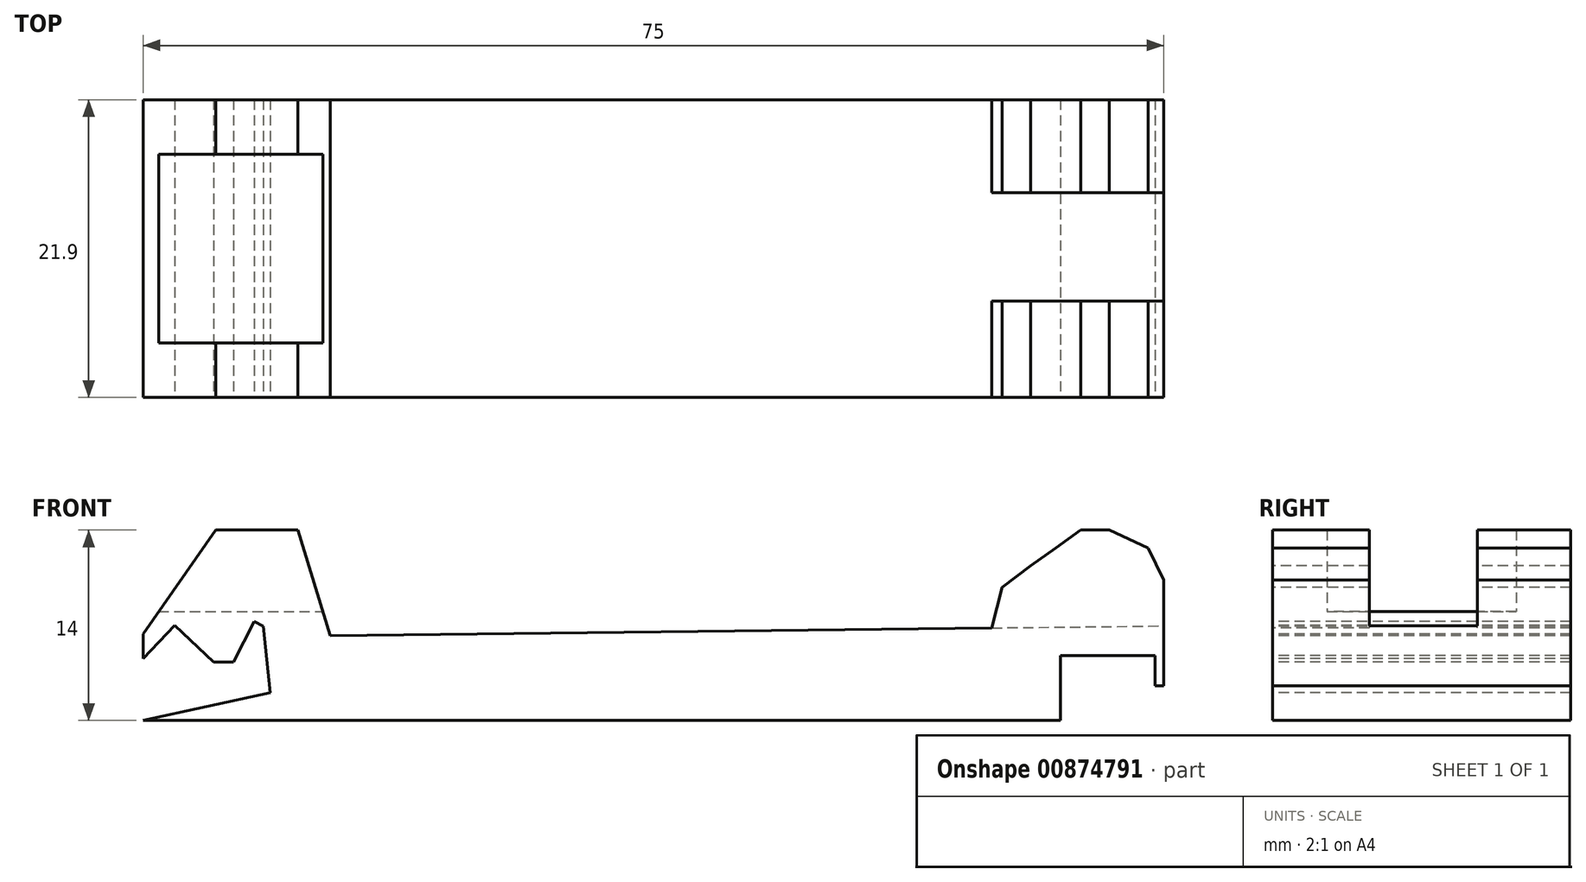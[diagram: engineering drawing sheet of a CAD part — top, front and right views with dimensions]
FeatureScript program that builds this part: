
annotation { "Feature Type Name" : "Feature", "Feature Type Description" : "" }
export const myFeature = defineFeature(function(context is Context, id is Id, definition is map)
    precondition{}
    {
        {
            var Q0;
            Q0=qCreatedBy(makeId("Top.planeOp"),FACE);
            var sketch = newSketch(context, id + "F0", { "sketchPlane" : qUnion([Q0])});
            skLineSegment(sketch, "E0.bottom", {"start": v(0, 0) * mm, "end": v(75, 0) * mm});
            skLineSegment(sketch, "E0.top", {"start": v(0, 21.9) * mm, "end": v(75, 21.9) * mm});
            skLineSegment(sketch, "E0.left", {"start": v(0, 0) * mm, "end": v(0, 21.9) * mm});
            skLineSegment(sketch, "E0.right", {"start": v(75, 0) * mm, "end": v(75, 21.9) * mm});
            skSolve(sketch);
        }
        {
            var Q0;
            Q0=makeQuery(id+"F0.imprint","IMPRINT",FACE,{"disambiguationData":[TD([[makeQuery(id+"F0.imprint","IMPRINT",EDGE,{"derivedFrom":sQuery(id+"F0.wireOp",EDGE,"E0.bottom")}),1.0]])]});
            extrude(context, id + "F1", {"entities" : qUnion([Q0]), "depth" : 14 * mm, "offsetDistance" : 25 * mm});
        }
        {
            var Q0;
            Q0=makeQuery(id+"F1.opExtrude","SWEPT_FACE",FACE,{"disambiguationData":[OSD([sQuery(id+"F0.wireOp",EDGE,"E0.bottom")])]});
            var sketch = newSketch(context, id + "F2", { "sketchPlane" : qUnion([Q0])});
            skLineSegment(sketch, "E1", {"start": v(0, 4.56) * mm, "end": v(2.32, 7) * mm});
            skLineSegment(sketch, "E2", {"start": v(2.32, 7) * mm, "end": v(5.16, 4.29) * mm});
            skLineSegment(sketch, "E3", {"start": v(5.16, 4.29) * mm, "end": v(6.63, 4.29) * mm});
            skLineSegment(sketch, "E4", {"start": v(6.63, 4.29) * mm, "end": v(8.16, 7.27) * mm});
            skLineSegment(sketch, "E5", {"start": v(8.16, 7.27) * mm, "end": v(8.82, 6.94) * mm});
            skLineSegment(sketch, "E6", {"start": v(8.82, 6.94) * mm, "end": v(9.34, 2.06) * mm});
            skLineSegment(sketch, "E7", {"start": v(9.34, 2.06) * mm, "end": v(0, 0) * mm});
            skLineSegment(sketch, "E8", {"start": v(67.4, 0) * mm, "end": v(67.4, 4.77) * mm});
            skLineSegment(sketch, "E9", {"start": v(67.4, 4.77) * mm, "end": v(74.34, 4.77) * mm});
            skLineSegment(sketch, "E10", {"start": v(74.34, 4.77) * mm, "end": v(74.34, 2.55) * mm});
            skLineSegment(sketch, "E11", {"start": v(74.34, 2.55) * mm, "end": v(75, 2.55) * mm});
            skLineSegment(sketch, "E12", {"start": v(0, 6.38) * mm, "end": v(5.33, 14) * mm});
            skLineSegment(sketch, "E13", {"start": v(5.33, 14) * mm, "end": v(11.37, 14) * mm});
            skLineSegment(sketch, "E14", {"start": v(11.37, 14) * mm, "end": v(13.74, 6.25) * mm});
            skLineSegment(sketch, "E15", {"start": v(13.74, 6.25) * mm, "end": v(62.36, 6.81) * mm});
            skLineSegment(sketch, "E16", {"start": v(62.36, 6.81) * mm, "end": v(63.1, 9.8) * mm});
            skLineSegment(sketch, "E17", {"start": v(63.1, 9.8) * mm, "end": v(65.2, 11.38) * mm});
            skLineSegment(sketch, "E18", {"start": v(65.2, 11.38) * mm, "end": v(67.05, 12.7) * mm});
            skLineSegment(sketch, "E19", {"start": v(67.05, 12.7) * mm, "end": v(68.89, 14) * mm});
            skLineSegment(sketch, "E20", {"start": v(68.89, 14) * mm, "end": v(70.99, 14) * mm});
            skLineSegment(sketch, "E21", {"start": v(70.99, 14) * mm, "end": v(73.87, 12.7) * mm});
            skLineSegment(sketch, "E22", {"start": v(73.87, 12.7) * mm, "end": v(75, 10.33) * mm});
            skLineSegment(sketch, "E23", {"start": v(75, 10.33) * mm, "end": v(75, 8.5) * mm});
            skSolve(sketch);
        }
        {
            var Q0;
            {var subQ0=sQuery(id+"F2.wireOp",EDGE,"E12");Q0=makeQuery(id+"F2.imprint","IMPRINT",FACE,{"disambiguationData":[TD([[makeQuery(id+"F2.imprint","IMPRINT",EDGE,{"derivedFrom":subQ0}),1.0]])]});}
            var Q1;
            {var subQ0=sQuery(id+"F2.wireOp",EDGE,"E14");Q1=makeQuery(id+"F2.imprint","IMPRINT",FACE,{"disambiguationData":[TD([[makeQuery(id+"F2.imprint","IMPRINT",EDGE,{"derivedFrom":subQ0}),1.0]])]});}
            var Q2;
            {var subQ0=sQuery(id+"F2.wireOp",EDGE,"E21");Q2=makeQuery(id+"F2.imprint","IMPRINT",FACE,{"disambiguationData":[TD([[makeQuery(id+"F2.imprint","IMPRINT",EDGE,{"derivedFrom":subQ0}),1.0]])]});}
            var Q3;
            {var subQ5=sQuery(id+"F2.wireOp",EDGE,"E8");Q3=makeQuery(id+"F2.imprint","IMPRINT",FACE,{"disambiguationData":[TD([[makeQuery(id+"F2.imprint","IMPRINT",EDGE,{"derivedFrom":subQ5}),-1.0]])]});}
            var Q4;
            {var subQ3=sQuery(id+"F2.wireOp",EDGE,"E1");Q4=makeQuery(id+"F2.imprint","IMPRINT",FACE,{"disambiguationData":[TD([[makeQuery(id+"F2.imprint","IMPRINT",EDGE,{"derivedFrom":subQ3}),-1.0]])]});}
            extrude(context, id + "F3", {"entities" : qUnion([Q0, Q1, Q2, Q3, Q4]), "operationType" : NewBodyOperationType.REMOVE, "endBound" : BoundingType.THROUGH_ALL, "oppositeDirection" : true, "depth" : 25 * mm, "offsetDistance" : 25 * mm});
        }
        {
            var Q0;
            Q0=makeQuery(id+"F3.boolean.opBoolean","COPY",FACE,{"derivedFrom":makeQuery(id+"F3.opExtrude","SWEPT_FACE",FACE,{"disambiguationData":[OSD([sQuery(id+"F2.wireOp",EDGE,"E15")])]})});
            var sketch = newSketch(context, id + "F4", { "sketchPlane" : qUnion([Q0])});
            skLineSegment(sketch, "E24.bottom", {"start": v(-8.24, 15.05) * mm, "end": v(86.41, 15.05) * mm});
            skLineSegment(sketch, "E24.top", {"start": v(-8.24, 7.1) * mm, "end": v(86.41, 7.1) * mm});
            skLineSegment(sketch, "E24.left", {"start": v(-8.24, 15.05) * mm, "end": v(-8.24, 7.1) * mm});
            skLineSegment(sketch, "E24.right", {"start": v(86.41, 15.05) * mm, "end": v(86.41, 7.1) * mm});
            skSolve(sketch);
        }
        {
            var Q0;
            {var subQ0=sQuery(id+"F4.wireOp",EDGE,"E24.right");Q0=makeQuery(id+"F4.imprint","IMPRINT",FACE,{"disambiguationData":[TD([[makeQuery(id+"F4.imprint","IMPRINT",EDGE,{"derivedFrom":subQ0}),-1.0]])]});}
            var Q1;
            {var subQ0=sQuery(id+"F4.wireOp",EDGE,"E24.bottom");var subQ1=sQuery(id+"F2.wireOp",EDGE,"E15");var subQ2=makeQuery(id+"F3.boolean.opBoolean","COPY",EDGE,{"derivedFrom":makeQuery(id+"F3.opExtrude","SWEPT_EDGE",EDGE,{"disambiguationData":[OSD([sQuery(id+"F2.wireOp",EDGE,"E14"),subQ1])]})});var subQ3=makeQuery(id+"F4.imprint","INTERSECT",VERTEX,{"derivedFrom":[subQ2,subQ0]});Q1=makeQuery(id+"F4.imprint","IMPRINT",FACE,{"disambiguationData":[TD([[makeQuery(id+"F4.imprint","IMPRINT",EDGE,{"disambiguationData":[TD([[subQ3,-1.0]])],"derivedFrom":subQ0}),-1.0]])]});}
            extrude(context, id + "F5", {"entities" : qUnion([Q0, Q1]), "operationType" : NewBodyOperationType.REMOVE, "depth" : 25 * mm, "offsetDistance" : 25 * mm});
        }
        {
            var Q0;
            {var subQ0=sQuery(id+"F0.wireOp",EDGE,"E0.bottom");var subQ1=sQuery(id+"F0.wireOp",EDGE,"E0.top");Q0=makeQuery(id+"F3.boolean.opBoolean","SPLIT",FACE,{"disambiguationData":[TD([makeQuery(id+"F3.opExtrude","SWEPT_FACE",FACE,{"disambiguationData":[OSD([sQuery(id+"F2.wireOp",EDGE,"E12")])]})])],"derivedFrom":makeQuery(id+"F1.opExtrude","CAP_FACE",FACE,{"disambiguationData":[OSD([subQ0,subQ1,sQuery(id+"F0.wireOp",EDGE,"E0.left"),sQuery(id+"F0.wireOp",EDGE,"E0.right")])],"isStart":false})});}
            var sketch = newSketch(context, id + "F6", { "sketchPlane" : qUnion([Q0])});
            skLineSegment(sketch, "E25.bottom", {"start": v(-5.03, 17.9) * mm, "end": v(19, 17.9) * mm});
            skLineSegment(sketch, "E25.top", {"start": v(-5.03, 4) * mm, "end": v(19, 4) * mm});
            skLineSegment(sketch, "E25.left", {"start": v(-5.03, 17.9) * mm, "end": v(-5.03, 4) * mm});
            skLineSegment(sketch, "E25.right", {"start": v(19, 17.9) * mm, "end": v(19, 4) * mm});
            skSolve(sketch);
        }
        {
            var Q0;
            {var subQ0=sQuery(id+"F6.wireOp",EDGE,"E25.right");Q0=makeQuery(id+"F6.imprint","IMPRINT",FACE,{"disambiguationData":[TD([[makeQuery(id+"F6.imprint","IMPRINT",EDGE,{"derivedFrom":subQ0}),-1.0]])]});}
            var Q1;
            {var subQ0=sQuery(id+"F6.wireOp",EDGE,"E25.bottom");var subQ1=sQuery(id+"F2.wireOp",EDGE,"E13");var subQ2=sQuery(id+"F0.wireOp",EDGE,"E0.bottom");var subQ3=makeQuery(id+"F3.boolean.opBoolean","COPY",EDGE,{"derivedFrom":makeQuery(id+"F3.opExtrude","SWEPT_EDGE",EDGE,{"disambiguationData":[OSD([subQ2,sQuery(id+"F2.wireOp",EDGE,"E12"),subQ1])]})});var subQ4=makeQuery(id+"F6.imprint","INTERSECT",VERTEX,{"derivedFrom":[subQ3,subQ0]});Q1=makeQuery(id+"F6.imprint","IMPRINT",FACE,{"disambiguationData":[TD([[makeQuery(id+"F6.imprint","IMPRINT",EDGE,{"disambiguationData":[TD([[subQ4,-1.0]])],"derivedFrom":subQ0}),-1.0]])]});}
            var Q2;
            {var subQ0=sQuery(id+"F6.wireOp",EDGE,"E25.left");Q2=makeQuery(id+"F6.imprint","IMPRINT",FACE,{"disambiguationData":[TD([[makeQuery(id+"F6.imprint","IMPRINT",EDGE,{"derivedFrom":subQ0}),1.0]])]});}
            extrude(context, id + "F7", {"entities" : qUnion([Q0, Q1, Q2]), "operationType" : NewBodyOperationType.REMOVE, "oppositeDirection" : true, "depth" : 6 * mm, "offsetDistance" : 25 * mm});
        }
    });
